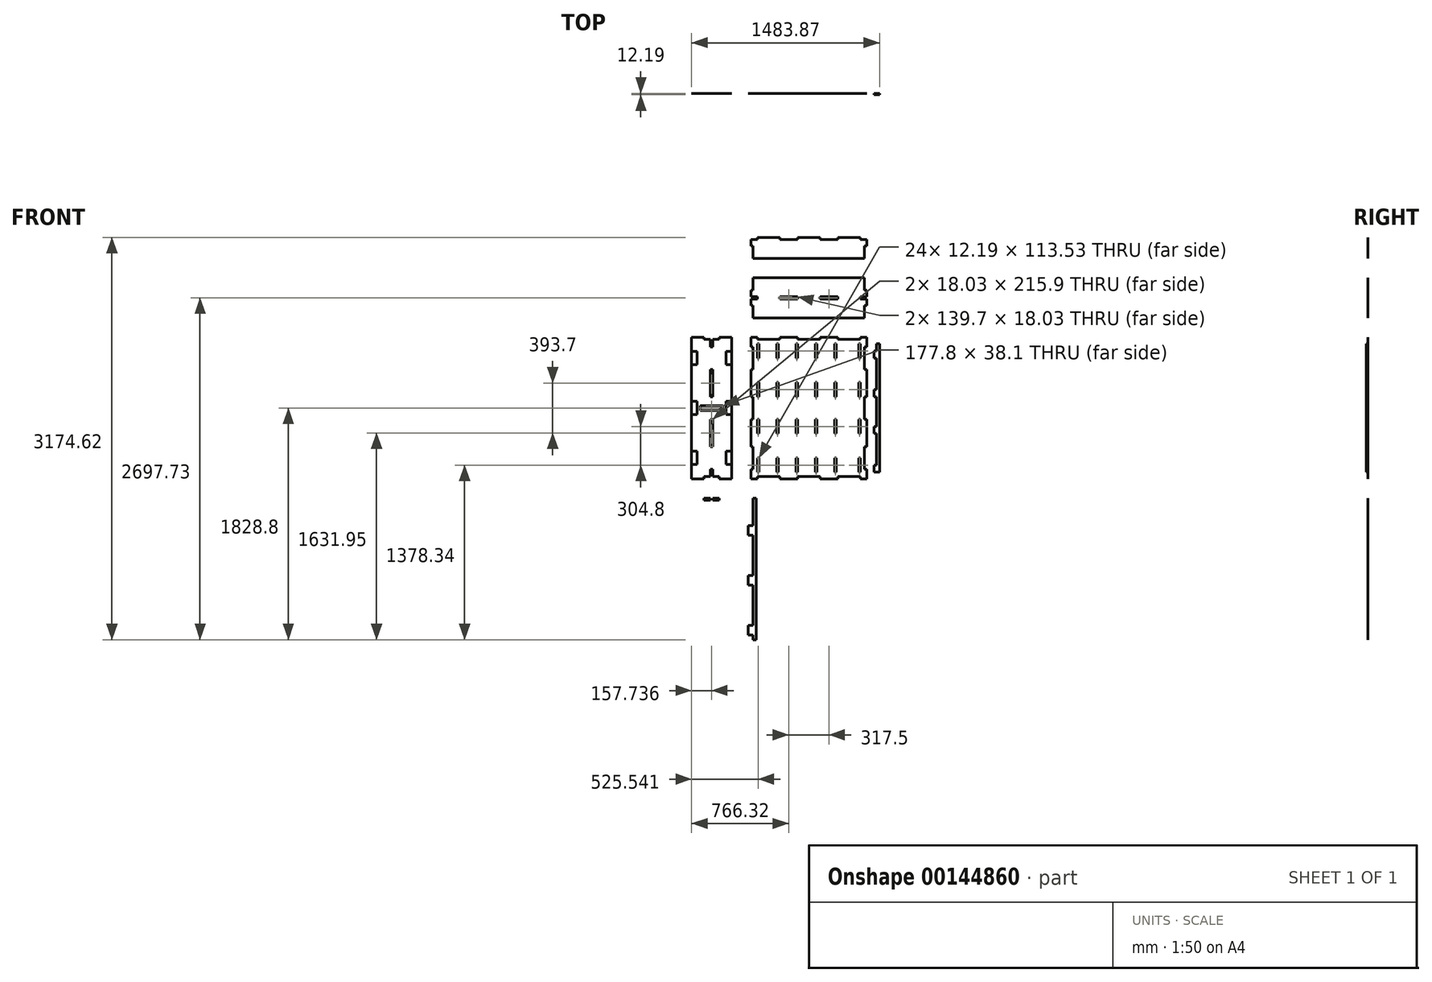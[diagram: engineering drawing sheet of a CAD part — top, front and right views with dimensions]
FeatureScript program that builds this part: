
annotation { "Feature Type Name" : "Feature", "Feature Type Description" : "" }
export const myFeature = defineFeature(function(context is Context, id is Id, definition is map)
    precondition{}
    {
        {
            assignVariable(context, id + "F0", {"name" : "ply34", "anyValue" : 0.71});
        }
        {
            var Q0;
            Q0=qCreatedBy(makeId("Front.planeOp"),FACE);
            var sketch = newSketch(context, id + "F1", { "sketchPlane" : qUnion([Q0])});
            skLineSegment(sketch, "E0.bottom", {"start": v(-457.2, 558.8) * mm, "end": v(457.2, 558.8) * mm});
            skLineSegment(sketch, "E0.top", {"start": v(-457.2, -558.8) * mm, "end": v(457.2, -558.8) * mm});
            skLineSegment(sketch, "E0.left", {"start": v(-457.2, 558.8) * mm, "end": v(-457.2, -558.8) * mm});
            skLineSegment(sketch, "E0.right", {"start": v(457.2, 558.8) * mm, "end": v(457.2, -558.8) * mm});
            skPoint(sketch, "E0.middle", {"position": v(0, 0) * mm});
            skLineSegment(sketch, "E1.bottom", {"start": v(-457.2, 482.6) * mm, "end": v(-439.17, 482.6) * mm});
            skLineSegment(sketch, "E1.top", {"start": v(-457.2, 304.8) * mm, "end": v(-439.17, 304.8) * mm});
            skLineSegment(sketch, "E1.left", {"start": v(-457.2, 482.6) * mm, "end": v(-457.2, 304.8) * mm});
            skLineSegment(sketch, "E1.right", {"start": v(-439.17, 482.6) * mm, "end": v(-439.17, 304.8) * mm});
            skLineSegment(sketch, "E2.bottom", {"start": v(-457.2, 88.9) * mm, "end": v(-439.17, 88.9) * mm});
            skLineSegment(sketch, "E2.top", {"start": v(-457.2, -88.9) * mm, "end": v(-439.17, -88.9) * mm});
            skLineSegment(sketch, "E2.left", {"start": v(-457.2, 88.9) * mm, "end": v(-457.2, -88.9) * mm});
            skLineSegment(sketch, "E2.right", {"start": v(-439.17, 88.9) * mm, "end": v(-439.17, -88.9) * mm});
            skPoint(sketch, "E3", {"position": v(-439.17, 0) * mm});
            skLineSegment(sketch, "E4", {"start": v(-457.2, 0) * mm, "end": v(457.2, 0) * mm, "construction": true});
            skLineSegment(sketch, "E5", {"start": v(0, 558.8) * mm, "end": v(0, -558.8) * mm, "construction": true});
            skLineSegment(sketch, "E6.MirrorCS", {"start": v(-457.2, -482.6) * mm, "end": v(-439.17, -482.6) * mm});
            skLineSegment(sketch, "E7.MirrorCS", {"start": v(-457.2, -304.8) * mm, "end": v(-439.17, -304.8) * mm});
            skLineSegment(sketch, "E8.MirrorCS", {"start": v(-457.2, -482.6) * mm, "end": v(-457.2, -304.8) * mm});
            skLineSegment(sketch, "E9.MirrorCS", {"start": v(-439.17, -482.6) * mm, "end": v(-439.17, -304.8) * mm});
            skLineSegment(sketch, "E10.MirrorCS", {"start": v(457.2, -88.9) * mm, "end": v(439.17, -88.9) * mm});
            skLineSegment(sketch, "E11.MirrorCS", {"start": v(457.2, 304.8) * mm, "end": v(439.17, 304.8) * mm});
            skLineSegment(sketch, "E12.MirrorCS", {"start": v(457.2, 482.6) * mm, "end": v(439.17, 482.6) * mm});
            skLineSegment(sketch, "E13.MirrorCS", {"start": v(457.2, 88.9) * mm, "end": v(439.17, 88.9) * mm});
            skLineSegment(sketch, "E14.MirrorCS", {"start": v(457.2, -304.8) * mm, "end": v(439.17, -304.8) * mm});
            skLineSegment(sketch, "E15.MirrorCS", {"start": v(457.2, -482.6) * mm, "end": v(439.17, -482.6) * mm});
            skLineSegment(sketch, "E16.MirrorCS", {"start": v(439.17, 88.9) * mm, "end": v(439.17, -88.9) * mm});
            skLineSegment(sketch, "E17.MirrorCS", {"start": v(457.2, 88.9) * mm, "end": v(457.2, -88.9) * mm});
            skLineSegment(sketch, "E18.MirrorCS", {"start": v(457.2, -482.6) * mm, "end": v(457.2, -304.8) * mm});
            skLineSegment(sketch, "E19.MirrorCS", {"start": v(439.17, -482.6) * mm, "end": v(439.17, -304.8) * mm});
            skLineSegment(sketch, "E20.MirrorCS", {"start": v(457.2, 482.6) * mm, "end": v(457.2, 304.8) * mm});
            skPoint(sketch, "E21.MirrorP", {"position": v(439.17, 0) * mm});
            skLineSegment(sketch, "E22.MirrorCS", {"start": v(439.17, 482.6) * mm, "end": v(439.17, 304.8) * mm});
            skLineSegment(sketch, "E23.bottom", {"start": v(-406.4, 558.8) * mm, "end": v(-228.6, 558.8) * mm});
            skLineSegment(sketch, "E23.top", {"start": v(-406.4, 540.77) * mm, "end": v(-228.6, 540.77) * mm});
            skLineSegment(sketch, "E23.left", {"start": v(-406.4, 558.8) * mm, "end": v(-406.4, 540.77) * mm});
            skLineSegment(sketch, "E23.right", {"start": v(-228.6, 558.8) * mm, "end": v(-228.6, 540.77) * mm});
            skLineSegment(sketch, "E24.bottom", {"start": v(-88.9, 558.8) * mm, "end": v(88.9, 558.8) * mm});
            skLineSegment(sketch, "E24.top", {"start": v(-88.9, 540.77) * mm, "end": v(88.9, 540.77) * mm});
            skLineSegment(sketch, "E24.left", {"start": v(-88.9, 558.8) * mm, "end": v(-88.9, 540.77) * mm});
            skLineSegment(sketch, "E24.right", {"start": v(88.9, 558.8) * mm, "end": v(88.9, 540.77) * mm});
            skPoint(sketch, "E25", {"position": v(0, 558.8) * mm});
            skLineSegment(sketch, "E26.MirrorCS", {"start": v(228.6, 558.8) * mm, "end": v(228.6, 540.77) * mm});
            skLineSegment(sketch, "E27.MirrorCS", {"start": v(406.4, 558.8) * mm, "end": v(406.4, 540.77) * mm});
            skLineSegment(sketch, "E28.MirrorCS", {"start": v(406.4, 540.77) * mm, "end": v(228.6, 540.77) * mm});
            skLineSegment(sketch, "E29.MirrorCS", {"start": v(406.4, 558.8) * mm, "end": v(228.6, 558.8) * mm});
            skLineSegment(sketch, "E30.MirrorCS", {"start": v(-88.9, -558.8) * mm, "end": v(88.9, -558.8) * mm});
            skLineSegment(sketch, "E31.MirrorCS", {"start": v(228.6, -558.8) * mm, "end": v(228.6, -540.77) * mm});
            skLineSegment(sketch, "E32.MirrorCS", {"start": v(-228.6, -558.8) * mm, "end": v(-228.6, -540.77) * mm});
            skLineSegment(sketch, "E33.MirrorCS", {"start": v(88.9, -558.8) * mm, "end": v(88.9, -540.77) * mm});
            skLineSegment(sketch, "E34.MirrorCS", {"start": v(-406.4, -558.8) * mm, "end": v(-406.4, -540.77) * mm});
            skLineSegment(sketch, "E35.MirrorCS", {"start": v(-88.9, -558.8) * mm, "end": v(-88.9, -540.77) * mm});
            skLineSegment(sketch, "E36.MirrorCS", {"start": v(406.4, -558.8) * mm, "end": v(406.4, -540.77) * mm});
            skLineSegment(sketch, "E37.MirrorCS", {"start": v(-406.4, -558.8) * mm, "end": v(-228.6, -558.8) * mm});
            skLineSegment(sketch, "E38.MirrorCS", {"start": v(-88.9, -540.77) * mm, "end": v(88.9, -540.77) * mm});
            skLineSegment(sketch, "E39.MirrorCS", {"start": v(-406.4, -540.77) * mm, "end": v(-228.6, -540.77) * mm});
            skLineSegment(sketch, "E40.MirrorCS", {"start": v(406.4, -558.8) * mm, "end": v(228.6, -558.8) * mm});
            skLineSegment(sketch, "E41.MirrorCS", {"start": v(406.4, -540.77) * mm, "end": v(228.6, -540.77) * mm});
            skPoint(sketch, "E42.MirrorP", {"position": v(0, -558.8) * mm});
            skLineSegment(sketch, "E43.bottom", {"start": v(-609.6, -558.8) * mm, "end": v(-925.07, -558.8) * mm});
            skLineSegment(sketch, "E43.top", {"start": v(-609.6, 558.8) * mm, "end": v(-925.07, 558.8) * mm});
            skLineSegment(sketch, "E43.left", {"start": v(-609.6, -558.8) * mm, "end": v(-609.6, 558.8) * mm});
            skLineSegment(sketch, "E43.right", {"start": v(-925.07, -558.8) * mm, "end": v(-925.07, 558.8) * mm});
            skLineSegment(sketch, "E44.bottom", {"start": v(-776.35, 558.8) * mm, "end": v(-758.32, 558.8) * mm});
            skLineSegment(sketch, "E44.top", {"start": v(-776.35, 482.6) * mm, "end": v(-758.32, 482.6) * mm});
            skLineSegment(sketch, "E44.left", {"start": v(-776.35, 558.8) * mm, "end": v(-776.35, 482.6) * mm});
            skLineSegment(sketch, "E44.right", {"start": v(-758.32, 558.8) * mm, "end": v(-758.32, 482.6) * mm});
            skPoint(sketch, "E45", {"position": v(-767.33, 558.8) * mm});
            skLineSegment(sketch, "E46.bottom", {"start": v(-776.35, 304.8) * mm, "end": v(-758.32, 304.8) * mm});
            skLineSegment(sketch, "E46.top", {"start": v(-776.35, 88.9) * mm, "end": v(-758.32, 88.9) * mm});
            skLineSegment(sketch, "E46.left", {"start": v(-776.35, 304.8) * mm, "end": v(-776.35, 88.9) * mm});
            skLineSegment(sketch, "E46.right", {"start": v(-758.32, 304.8) * mm, "end": v(-758.32, 88.9) * mm});
            skLineSegment(sketch, "E47.bottom", {"start": v(-776.35, -88.9) * mm, "end": v(-758.32, -88.9) * mm});
            skLineSegment(sketch, "E47.top", {"start": v(-776.35, -304.8) * mm, "end": v(-758.32, -304.8) * mm});
            skLineSegment(sketch, "E47.left", {"start": v(-776.35, -88.9) * mm, "end": v(-776.35, -304.8) * mm});
            skLineSegment(sketch, "E47.right", {"start": v(-758.32, -88.9) * mm, "end": v(-758.32, -304.8) * mm});
            skLineSegment(sketch, "E48.bottom", {"start": v(-776.35, -482.6) * mm, "end": v(-758.32, -482.6) * mm});
            skLineSegment(sketch, "E48.top", {"start": v(-776.35, -558.8) * mm, "end": v(-758.32, -558.8) * mm});
            skLineSegment(sketch, "E48.left", {"start": v(-776.35, -482.6) * mm, "end": v(-776.35, -558.8) * mm});
            skLineSegment(sketch, "E48.right", {"start": v(-758.32, -482.6) * mm, "end": v(-758.32, -558.8) * mm});
            skLineSegment(sketch, "E49.bottom", {"start": v(-776.35, 558.8) * mm, "end": v(-827.15, 558.8) * mm});
            skLineSegment(sketch, "E49.top", {"start": v(-776.35, 540.77) * mm, "end": v(-827.15, 540.77) * mm});
            skLineSegment(sketch, "E49.left", {"start": v(-776.35, 558.8) * mm, "end": v(-776.35, 540.77) * mm});
            skLineSegment(sketch, "E49.right", {"start": v(-827.15, 558.8) * mm, "end": v(-827.15, 540.77) * mm});
            skLineSegment(sketch, "E50.bottom", {"start": v(-758.32, 558.8) * mm, "end": v(-707.52, 558.8) * mm});
            skLineSegment(sketch, "E50.top", {"start": v(-758.32, 540.77) * mm, "end": v(-707.52, 540.77) * mm});
            skLineSegment(sketch, "E50.left", {"start": v(-758.32, 558.8) * mm, "end": v(-758.32, 540.77) * mm});
            skLineSegment(sketch, "E50.right", {"start": v(-707.52, 558.8) * mm, "end": v(-707.52, 540.77) * mm});
            skLineSegment(sketch, "E51.MirrorCS", {"start": v(-758.32, -540.77) * mm, "end": v(-707.52, -540.77) * mm});
            skLineSegment(sketch, "E52.MirrorCS", {"start": v(-758.32, -558.8) * mm, "end": v(-707.52, -558.8) * mm});
            skLineSegment(sketch, "E53.MirrorCS", {"start": v(-758.32, -558.8) * mm, "end": v(-758.32, -540.77) * mm});
            skLineSegment(sketch, "E54.MirrorCS", {"start": v(-827.15, -558.8) * mm, "end": v(-827.15, -540.77) * mm});
            skLineSegment(sketch, "E55.MirrorCS", {"start": v(-776.35, -540.77) * mm, "end": v(-827.15, -540.77) * mm});
            skPoint(sketch, "E56.MirrorP", {"position": v(-767.33, -558.8) * mm});
            skLineSegment(sketch, "E57.MirrorCS", {"start": v(-776.35, -558.8) * mm, "end": v(-776.35, -540.77) * mm});
            skLineSegment(sketch, "E58.MirrorCS", {"start": v(-776.35, -558.8) * mm, "end": v(-827.15, -558.8) * mm});
            skLineSegment(sketch, "E59.MirrorCS", {"start": v(-707.52, -558.8) * mm, "end": v(-707.52, -540.77) * mm});
            skLineSegment(sketch, "E60.bottom", {"start": v(-439.17, 1026.67) * mm, "end": v(439.17, 1026.67) * mm});
            skLineSegment(sketch, "E60.top", {"start": v(-439.17, 711.2) * mm, "end": v(439.17, 711.2) * mm});
            skLineSegment(sketch, "E60.left", {"start": v(-439.17, 1026.67) * mm, "end": v(-439.17, 711.2) * mm});
            skLineSegment(sketch, "E60.right", {"start": v(439.17, 1026.67) * mm, "end": v(439.17, 711.2) * mm});
            skLineSegment(sketch, "E61.bottom", {"start": v(-439.17, 877.95) * mm, "end": v(-457.2, 877.95) * mm});
            skLineSegment(sketch, "E61.top", {"start": v(-439.17, 928.75) * mm, "end": v(-457.2, 928.75) * mm});
            skLineSegment(sketch, "E61.left", {"start": v(-439.17, 877.95) * mm, "end": v(-439.17, 928.75) * mm});
            skLineSegment(sketch, "E61.right", {"start": v(-457.2, 877.95) * mm, "end": v(-457.2, 928.75) * mm});
            skLineSegment(sketch, "E62.bottom", {"start": v(-439.17, 859.92) * mm, "end": v(-457.2, 859.92) * mm});
            skLineSegment(sketch, "E62.top", {"start": v(-439.17, 809.12) * mm, "end": v(-457.2, 809.12) * mm});
            skLineSegment(sketch, "E62.left", {"start": v(-439.17, 859.92) * mm, "end": v(-439.17, 809.12) * mm});
            skLineSegment(sketch, "E62.right", {"start": v(-457.2, 859.92) * mm, "end": v(-457.2, 809.12) * mm});
            skLineSegment(sketch, "E63", {"start": v(-448.18, 877.95) * mm, "end": v(-448.18, 859.92) * mm, "construction": true});
            skPoint(sketch, "E64", {"position": v(-448.18, 868.93) * mm});
            skPoint(sketch, "E65", {"position": v(-439.17, 868.93) * mm});
            skLineSegment(sketch, "E66.bottom", {"start": v(-439.17, 877.95) * mm, "end": v(-406.4, 877.95) * mm});
            skLineSegment(sketch, "E66.top", {"start": v(-439.17, 859.92) * mm, "end": v(-406.4, 859.92) * mm});
            skLineSegment(sketch, "E66.left", {"start": v(-439.17, 877.95) * mm, "end": v(-439.17, 859.92) * mm});
            skLineSegment(sketch, "E66.right", {"start": v(-406.4, 877.95) * mm, "end": v(-406.4, 859.92) * mm});
            skLineSegment(sketch, "E67.bottom", {"start": v(-228.6, 877.95) * mm, "end": v(-88.9, 877.95) * mm});
            skLineSegment(sketch, "E67.top", {"start": v(-228.6, 859.92) * mm, "end": v(-88.9, 859.92) * mm});
            skLineSegment(sketch, "E67.left", {"start": v(-228.6, 877.95) * mm, "end": v(-228.6, 859.92) * mm});
            skLineSegment(sketch, "E67.right", {"start": v(-88.9, 877.95) * mm, "end": v(-88.9, 859.92) * mm});
            skLineSegment(sketch, "E68.bottom", {"start": v(88.9, 877.95) * mm, "end": v(228.6, 877.95) * mm});
            skLineSegment(sketch, "E68.top", {"start": v(88.9, 859.92) * mm, "end": v(228.6, 859.92) * mm});
            skLineSegment(sketch, "E68.left", {"start": v(88.9, 877.95) * mm, "end": v(88.9, 859.92) * mm});
            skLineSegment(sketch, "E68.right", {"start": v(228.6, 877.95) * mm, "end": v(228.6, 859.92) * mm});
            skLineSegment(sketch, "E69.MirrorCS", {"start": v(439.17, 877.95) * mm, "end": v(439.17, 859.92) * mm});
            skLineSegment(sketch, "E70.MirrorCS", {"start": v(439.17, 877.95) * mm, "end": v(457.2, 877.95) * mm});
            skLineSegment(sketch, "E71.MirrorCS", {"start": v(406.4, 877.95) * mm, "end": v(406.4, 859.92) * mm});
            skLineSegment(sketch, "E72.MirrorCS", {"start": v(439.17, 928.75) * mm, "end": v(457.2, 928.75) * mm});
            skLineSegment(sketch, "E73.MirrorCS", {"start": v(448.18, 877.95) * mm, "end": v(448.18, 859.92) * mm, "construction": true});
            skLineSegment(sketch, "E74.MirrorCS", {"start": v(439.17, 809.12) * mm, "end": v(457.2, 809.12) * mm});
            skLineSegment(sketch, "E75.MirrorCS", {"start": v(439.17, 859.92) * mm, "end": v(457.2, 859.92) * mm});
            skLineSegment(sketch, "E76.MirrorCS", {"start": v(439.17, 877.95) * mm, "end": v(406.4, 877.95) * mm});
            skLineSegment(sketch, "E77.MirrorCS", {"start": v(439.17, 859.92) * mm, "end": v(406.4, 859.92) * mm});
            skLineSegment(sketch, "E78.MirrorCS", {"start": v(439.17, 877.95) * mm, "end": v(439.17, 928.75) * mm});
            skLineSegment(sketch, "E79.MirrorCS", {"start": v(439.17, 859.92) * mm, "end": v(439.17, 809.12) * mm});
            skLineSegment(sketch, "E80.MirrorCS", {"start": v(457.2, 877.95) * mm, "end": v(457.2, 928.75) * mm});
            skPoint(sketch, "E81.MirrorP", {"position": v(439.17, 868.93) * mm});
            skLineSegment(sketch, "E82.MirrorCS", {"start": v(457.2, 859.92) * mm, "end": v(457.2, 809.12) * mm});
            skPoint(sketch, "E83.MirrorP", {"position": v(448.18, 868.93) * mm});
            skLineSegment(sketch, "E84", {"start": v(-767.33, -558.8) * mm, "end": v(-767.33, 558.8) * mm, "construction": true});
            skLineSegment(sketch, "E85", {"start": v(439.17, 1102.87) * mm, "end": v(-439.17, 1102.87) * mm, "construction": true});
            skLineSegment(sketch, "E86.MirrorCS", {"start": v(-439.17, 1179.07) * mm, "end": v(439.17, 1179.07) * mm});
            skLineSegment(sketch, "E87.MirrorCS", {"start": v(-439.17, 1179.07) * mm, "end": v(-439.17, 1345.82) * mm});
            skLineSegment(sketch, "E88.MirrorCS", {"start": v(439.17, 1179.07) * mm, "end": v(439.17, 1345.82) * mm});
            skLineSegment(sketch, "E89.MirrorCS", {"start": v(228.6, 1327.78) * mm, "end": v(228.6, 1345.82) * mm});
            skLineSegment(sketch, "E90.MirrorCS", {"start": v(-228.6, 1327.78) * mm, "end": v(-228.6, 1345.82) * mm});
            skLineSegment(sketch, "E91.MirrorCS", {"start": v(-88.9, 1327.78) * mm, "end": v(-88.9, 1345.82) * mm});
            skLineSegment(sketch, "E92.MirrorCS", {"start": v(88.9, 1327.78) * mm, "end": v(88.9, 1345.82) * mm});
            skLineSegment(sketch, "E93.MirrorCS", {"start": v(-228.6, 1345.82) * mm, "end": v(-88.9, 1345.82) * mm});
            skLineSegment(sketch, "E94.MirrorCS", {"start": v(-228.6, 1327.78) * mm, "end": v(-88.9, 1327.78) * mm});
            skLineSegment(sketch, "E95.MirrorCS", {"start": v(88.9, 1345.82) * mm, "end": v(228.6, 1345.82) * mm});
            skLineSegment(sketch, "E96.MirrorCS", {"start": v(88.9, 1327.78) * mm, "end": v(228.6, 1327.78) * mm});
            skLineSegment(sketch, "E97.MirrorCS", {"start": v(439.17, 1276.98) * mm, "end": v(457.2, 1276.98) * mm});
            skLineSegment(sketch, "E98.MirrorCS", {"start": v(457.2, 1327.78) * mm, "end": v(457.2, 1276.98) * mm});
            skLineSegment(sketch, "E99.MirrorCS", {"start": v(439.17, 1327.78) * mm, "end": v(457.2, 1327.78) * mm});
            skLineSegment(sketch, "E100.MirrorCS", {"start": v(439.17, 1327.78) * mm, "end": v(406.4, 1327.78) * mm});
            skLineSegment(sketch, "E101.MirrorCS", {"start": v(406.4, 1327.78) * mm, "end": v(406.4, 1345.82) * mm});
            skLineSegment(sketch, "E102.MirrorCS", {"start": v(439.17, 1345.82) * mm, "end": v(406.4, 1345.82) * mm});
            skLineSegment(sketch, "E103.MirrorCS", {"start": v(-439.17, 1276.98) * mm, "end": v(-457.2, 1276.98) * mm});
            skLineSegment(sketch, "E104.MirrorCS", {"start": v(-457.2, 1327.78) * mm, "end": v(-457.2, 1276.98) * mm});
            skLineSegment(sketch, "E105.MirrorCS", {"start": v(-439.17, 1327.78) * mm, "end": v(-457.2, 1327.78) * mm});
            skLineSegment(sketch, "E106.MirrorCS", {"start": v(-439.17, 1327.78) * mm, "end": v(-406.4, 1327.78) * mm});
            skLineSegment(sketch, "E107.MirrorCS", {"start": v(-406.4, 1327.78) * mm, "end": v(-406.4, 1345.82) * mm});
            skLineSegment(sketch, "E108.MirrorCS", {"start": v(-439.17, 1345.82) * mm, "end": v(-406.4, 1345.82) * mm});
            skLineSegment(sketch, "E109", {"start": v(-406.4, 1345.82) * mm, "end": v(-228.6, 1345.82) * mm});
            skLineSegment(sketch, "E110", {"start": v(-88.9, 1345.82) * mm, "end": v(88.9, 1345.82) * mm});
            skLineSegment(sketch, "E111", {"start": v(228.6, 1345.82) * mm, "end": v(406.4, 1345.82) * mm});
            skLineSegment(sketch, "E112.bottom", {"start": v(-609.6, 52.07) * mm, "end": v(-653.31, 52.07) * mm});
            skLineSegment(sketch, "E112.top", {"start": v(-609.6, -52.07) * mm, "end": v(-653.31, -52.07) * mm});
            skLineSegment(sketch, "E112.left", {"start": v(-609.6, 52.07) * mm, "end": v(-609.6, -52.07) * mm});
            skLineSegment(sketch, "E112.right", {"start": v(-653.31, 52.07) * mm, "end": v(-653.31, -52.07) * mm});
            skPoint(sketch, "E113", {"position": v(-609.6, 0) * mm});
            skLineSegment(sketch, "E114", {"start": v(-758.32, 482.6) * mm, "end": v(-758.32, 304.8) * mm, "construction": true});
            skLineSegment(sketch, "E115.bottom", {"start": v(-653.31, 341.63) * mm, "end": v(-609.6, 341.63) * mm});
            skLineSegment(sketch, "E115.top", {"start": v(-653.31, 445.77) * mm, "end": v(-609.6, 445.77) * mm});
            skLineSegment(sketch, "E115.left", {"start": v(-653.31, 341.63) * mm, "end": v(-653.31, 445.77) * mm});
            skLineSegment(sketch, "E115.right", {"start": v(-609.6, 341.63) * mm, "end": v(-609.6, 445.77) * mm});
            skPoint(sketch, "E115.middle", {"position": v(-631.46, 393.7) * mm});
            skPoint(sketch, "E115.middle.positionSnap0", {"position": v(-631.46, 52.07) * mm});
            skPoint(sketch, "E115.middle.positionSnap1", {"position": v(-758.32, 393.7) * mm});
            skPoint(sketch, "E115.centerSnap0", {"position": v(-631.46, 52.07) * mm});
            skPoint(sketch, "E115.centerSnap1", {"position": v(-758.32, 393.7) * mm});
            skLineSegment(sketch, "E116.MirrorCS", {"start": v(-653.31, -341.63) * mm, "end": v(-609.6, -341.63) * mm});
            skLineSegment(sketch, "E117.MirrorCS", {"start": v(-653.31, -445.77) * mm, "end": v(-609.6, -445.77) * mm});
            skLineSegment(sketch, "E118.MirrorCS", {"start": v(-653.31, -341.63) * mm, "end": v(-653.31, -445.77) * mm});
            skPoint(sketch, "E119.MirrorP", {"position": v(-631.46, -393.7) * mm});
            skLineSegment(sketch, "E120.MirrorCS", {"start": v(-609.6, -341.63) * mm, "end": v(-609.6, -445.77) * mm});
            skLineSegment(sketch, "E121.MirrorCS", {"start": v(-881.35, -445.77) * mm, "end": v(-925.07, -445.77) * mm});
            skLineSegment(sketch, "E122.MirrorCS", {"start": v(-881.35, -341.63) * mm, "end": v(-925.07, -341.63) * mm});
            skLineSegment(sketch, "E123.MirrorCS", {"start": v(-881.35, 445.77) * mm, "end": v(-925.07, 445.77) * mm});
            skLineSegment(sketch, "E124.MirrorCS", {"start": v(-881.35, 341.63) * mm, "end": v(-925.07, 341.63) * mm});
            skLineSegment(sketch, "E125.MirrorCS", {"start": v(-925.07, -52.07) * mm, "end": v(-881.35, -52.07) * mm});
            skLineSegment(sketch, "E126.MirrorCS", {"start": v(-925.07, 52.07) * mm, "end": v(-881.35, 52.07) * mm});
            skLineSegment(sketch, "E127.MirrorCS", {"start": v(-925.07, -341.63) * mm, "end": v(-925.07, -445.77) * mm});
            skPoint(sketch, "E128.MirrorP", {"position": v(-903.21, 52.07) * mm});
            skLineSegment(sketch, "E129.MirrorCS", {"start": v(-881.35, -341.63) * mm, "end": v(-881.35, -445.77) * mm});
            skLineSegment(sketch, "E130.MirrorCS", {"start": v(-925.07, 341.63) * mm, "end": v(-925.07, 445.77) * mm});
            skLineSegment(sketch, "E131.MirrorCS", {"start": v(-881.35, 341.63) * mm, "end": v(-881.35, 445.77) * mm});
            skLineSegment(sketch, "E132.MirrorCS", {"start": v(-925.07, 52.07) * mm, "end": v(-925.07, -52.07) * mm});
            skLineSegment(sketch, "E133.MirrorCS", {"start": v(-881.35, 52.07) * mm, "end": v(-881.35, -52.07) * mm});
            skPoint(sketch, "E134.MirrorP", {"position": v(-903.21, 393.7) * mm});
            skPoint(sketch, "E135.MirrorP", {"position": v(-925.07, 0) * mm});
            skPoint(sketch, "E136.MirrorP", {"position": v(-903.21, -393.7) * mm});
            skLineSegment(sketch, "E137.bottom", {"start": v(-405.63, 507.23) * mm, "end": v(405.63, 507.23) * mm, "construction": true});
            skLineSegment(sketch, "E137.top", {"start": v(-405.63, -507.23) * mm, "end": v(405.63, -507.23) * mm, "construction": true});
            skLineSegment(sketch, "E137.left", {"start": v(-405.63, 507.23) * mm, "end": v(-405.63, -507.23) * mm, "construction": true});
            skLineSegment(sketch, "E137.right", {"start": v(405.63, 507.23) * mm, "end": v(405.63, -507.23) * mm, "construction": true});
            skLineSegment(sketch, "E138.0", {"start": v(-393.43, 495.03) * mm, "end": v(393.43, 495.03) * mm, "construction": true});
            skLineSegment(sketch, "E138.1", {"start": v(-393.43, 495.03) * mm, "end": v(-393.43, -495.03) * mm, "construction": true});
            skLineSegment(sketch, "E138.2", {"start": v(-393.43, -495.03) * mm, "end": v(393.43, -495.03) * mm, "construction": true});
            skLineSegment(sketch, "E138.3", {"start": v(393.43, 495.03) * mm, "end": v(393.43, -495.03) * mm, "construction": true});
            skPoint(sketch, "E139.oppositeSnap0", {"position": v(-439.17, 393.7) * mm});
            skLineSegment(sketch, "E139.bottom", {"start": v(-405.63, 507.23) * mm, "end": v(-393.43, 507.23) * mm});
            skLineSegment(sketch, "E139.top", {"start": v(-405.63, 393.7) * mm, "end": v(-393.43, 393.7) * mm});
            skLineSegment(sketch, "E139.left", {"start": v(-405.63, 507.23) * mm, "end": v(-405.63, 393.7) * mm});
            skLineSegment(sketch, "E139.right", {"start": v(-393.43, 507.23) * mm, "end": v(-393.43, 393.7) * mm});
            skPoint(sketch, "E140.oppositeSnap0", {"position": v(-439.17, -393.7) * mm});
            skLineSegment(sketch, "E140.bottom", {"start": v(-405.63, -507.23) * mm, "end": v(-393.43, -507.23) * mm});
            skLineSegment(sketch, "E140.top", {"start": v(-405.63, -393.7) * mm, "end": v(-393.43, -393.7) * mm});
            skLineSegment(sketch, "E140.left", {"start": v(-405.63, -507.23) * mm, "end": v(-405.63, -393.7) * mm});
            skLineSegment(sketch, "E140.right", {"start": v(-393.43, -507.23) * mm, "end": v(-393.43, -393.7) * mm});
            skLineSegment(sketch, "E141.bottom", {"start": v(-405.63, 88.9) * mm, "end": v(-393.43, 88.9) * mm});
            skLineSegment(sketch, "E141.top", {"start": v(-405.63, 202.43) * mm, "end": v(-393.43, 202.43) * mm});
            skLineSegment(sketch, "E141.left", {"start": v(-405.63, 88.9) * mm, "end": v(-405.63, 202.43) * mm});
            skLineSegment(sketch, "E141.right", {"start": v(-393.43, 88.9) * mm, "end": v(-393.43, 202.43) * mm});
            skLineSegment(sketch, "E142.bottom", {"start": v(-405.63, -88.9) * mm, "end": v(-393.43, -88.9) * mm});
            skLineSegment(sketch, "E142.top", {"start": v(-405.63, -202.43) * mm, "end": v(-393.43, -202.43) * mm});
            skLineSegment(sketch, "E142.left", {"start": v(-405.63, -88.9) * mm, "end": v(-405.63, -202.43) * mm});
            skLineSegment(sketch, "E142.right", {"start": v(-393.43, -88.9) * mm, "end": v(-393.43, -202.43) * mm});
            skLineSegment(sketch, "E143.1.0.0", {"start": v(-253.23, -507.23) * mm, "end": v(-253.23, -393.7) * mm});
            skLineSegment(sketch, "E143.1.0.1", {"start": v(-241.03, -507.23) * mm, "end": v(-241.03, -393.7) * mm});
            skLineSegment(sketch, "E143.1.0.2", {"start": v(-253.23, -507.23) * mm, "end": v(-241.03, -507.23) * mm});
            skLineSegment(sketch, "E143.1.0.3", {"start": v(-253.23, -393.7) * mm, "end": v(-241.03, -393.7) * mm});
            skLineSegment(sketch, "E143.1.0.4", {"start": v(-253.23, -88.9) * mm, "end": v(-241.03, -88.9) * mm});
            skLineSegment(sketch, "E143.1.0.5", {"start": v(-253.23, -202.43) * mm, "end": v(-241.03, -202.43) * mm});
            skLineSegment(sketch, "E143.1.0.6", {"start": v(-253.23, -88.9) * mm, "end": v(-253.23, -202.43) * mm});
            skLineSegment(sketch, "E143.1.0.7", {"start": v(-241.03, -88.9) * mm, "end": v(-241.03, -202.43) * mm});
            skLineSegment(sketch, "E143.1.0.8", {"start": v(-253.23, 88.9) * mm, "end": v(-253.23, 202.43) * mm});
            skLineSegment(sketch, "E143.1.0.9", {"start": v(-241.03, 88.9) * mm, "end": v(-241.03, 202.43) * mm});
            skLineSegment(sketch, "E143.1.0.10", {"start": v(-253.23, 88.9) * mm, "end": v(-241.03, 88.9) * mm});
            skLineSegment(sketch, "E143.1.0.11", {"start": v(-253.23, 202.43) * mm, "end": v(-241.03, 202.43) * mm});
            skLineSegment(sketch, "E143.1.0.12", {"start": v(-253.23, 507.23) * mm, "end": v(-241.03, 507.23) * mm});
            skLineSegment(sketch, "E143.1.0.13", {"start": v(-253.23, 393.7) * mm, "end": v(-241.03, 393.7) * mm});
            skLineSegment(sketch, "E143.1.0.14", {"start": v(-253.23, 507.23) * mm, "end": v(-253.23, 393.7) * mm});
            skLineSegment(sketch, "E143.1.0.15", {"start": v(-241.03, 507.23) * mm, "end": v(-241.03, 393.7) * mm});
            skLineSegment(sketch, "E143.2.0.0", {"start": v(-100.83, -507.23) * mm, "end": v(-100.83, -393.7) * mm});
            skLineSegment(sketch, "E143.2.0.1", {"start": v(-88.63, -507.23) * mm, "end": v(-88.63, -393.7) * mm});
            skLineSegment(sketch, "E143.2.0.2", {"start": v(-100.83, -507.23) * mm, "end": v(-88.63, -507.23) * mm});
            skLineSegment(sketch, "E143.2.0.3", {"start": v(-100.83, -393.7) * mm, "end": v(-88.63, -393.7) * mm});
            skLineSegment(sketch, "E143.2.0.4", {"start": v(-100.83, -88.9) * mm, "end": v(-88.63, -88.9) * mm});
            skLineSegment(sketch, "E143.2.0.5", {"start": v(-100.83, -202.43) * mm, "end": v(-88.63, -202.43) * mm});
            skLineSegment(sketch, "E143.2.0.6", {"start": v(-100.83, -88.9) * mm, "end": v(-100.83, -202.43) * mm});
            skLineSegment(sketch, "E143.2.0.7", {"start": v(-88.63, -88.9) * mm, "end": v(-88.63, -202.43) * mm});
            skLineSegment(sketch, "E143.2.0.8", {"start": v(-100.83, 88.9) * mm, "end": v(-100.83, 202.43) * mm});
            skLineSegment(sketch, "E143.2.0.9", {"start": v(-88.63, 88.9) * mm, "end": v(-88.63, 202.43) * mm});
            skLineSegment(sketch, "E143.2.0.10", {"start": v(-100.83, 88.9) * mm, "end": v(-88.63, 88.9) * mm});
            skLineSegment(sketch, "E143.2.0.11", {"start": v(-100.83, 202.43) * mm, "end": v(-88.63, 202.43) * mm});
            skLineSegment(sketch, "E143.2.0.12", {"start": v(-100.83, 507.23) * mm, "end": v(-88.63, 507.23) * mm});
            skLineSegment(sketch, "E143.2.0.13", {"start": v(-100.83, 393.7) * mm, "end": v(-88.63, 393.7) * mm});
            skLineSegment(sketch, "E143.2.0.14", {"start": v(-100.83, 507.23) * mm, "end": v(-100.83, 393.7) * mm});
            skLineSegment(sketch, "E143.2.0.15", {"start": v(-88.63, 507.23) * mm, "end": v(-88.63, 393.7) * mm});
            skLineSegment(sketch, "E143.3.0.0", {"start": v(51.57, -507.23) * mm, "end": v(51.57, -393.7) * mm});
            skLineSegment(sketch, "E143.3.0.1", {"start": v(63.77, -507.23) * mm, "end": v(63.77, -393.7) * mm});
            skLineSegment(sketch, "E143.3.0.2", {"start": v(51.57, -507.23) * mm, "end": v(63.77, -507.23) * mm});
            skLineSegment(sketch, "E143.3.0.3", {"start": v(51.57, -393.7) * mm, "end": v(63.77, -393.7) * mm});
            skLineSegment(sketch, "E143.3.0.4", {"start": v(51.57, -88.9) * mm, "end": v(63.77, -88.9) * mm});
            skLineSegment(sketch, "E143.3.0.5", {"start": v(51.57, -202.43) * mm, "end": v(63.77, -202.43) * mm});
            skLineSegment(sketch, "E143.3.0.6", {"start": v(51.57, -88.9) * mm, "end": v(51.57, -202.43) * mm});
            skLineSegment(sketch, "E143.3.0.7", {"start": v(63.77, -88.9) * mm, "end": v(63.77, -202.43) * mm});
            skLineSegment(sketch, "E143.3.0.8", {"start": v(51.57, 88.9) * mm, "end": v(51.57, 202.43) * mm});
            skLineSegment(sketch, "E143.3.0.9", {"start": v(63.77, 88.9) * mm, "end": v(63.77, 202.43) * mm});
            skLineSegment(sketch, "E143.3.0.10", {"start": v(51.57, 88.9) * mm, "end": v(63.77, 88.9) * mm});
            skLineSegment(sketch, "E143.3.0.11", {"start": v(51.57, 202.43) * mm, "end": v(63.77, 202.43) * mm});
            skLineSegment(sketch, "E143.3.0.12", {"start": v(51.57, 507.23) * mm, "end": v(63.77, 507.23) * mm});
            skLineSegment(sketch, "E143.3.0.13", {"start": v(51.57, 393.7) * mm, "end": v(63.77, 393.7) * mm});
            skLineSegment(sketch, "E143.3.0.14", {"start": v(51.57, 507.23) * mm, "end": v(51.57, 393.7) * mm});
            skLineSegment(sketch, "E143.3.0.15", {"start": v(63.77, 507.23) * mm, "end": v(63.77, 393.7) * mm});
            skLineSegment(sketch, "E143.4.0.0", {"start": v(203.97, -507.23) * mm, "end": v(203.97, -393.7) * mm});
            skLineSegment(sketch, "E143.4.0.1", {"start": v(216.17, -507.23) * mm, "end": v(216.17, -393.7) * mm});
            skLineSegment(sketch, "E143.4.0.2", {"start": v(203.97, -507.23) * mm, "end": v(216.17, -507.23) * mm});
            skLineSegment(sketch, "E143.4.0.3", {"start": v(203.97, -393.7) * mm, "end": v(216.17, -393.7) * mm});
            skLineSegment(sketch, "E143.4.0.4", {"start": v(203.97, -88.9) * mm, "end": v(216.17, -88.9) * mm});
            skLineSegment(sketch, "E143.4.0.5", {"start": v(203.97, -202.43) * mm, "end": v(216.17, -202.43) * mm});
            skLineSegment(sketch, "E143.4.0.6", {"start": v(203.97, -88.9) * mm, "end": v(203.97, -202.43) * mm});
            skLineSegment(sketch, "E143.4.0.7", {"start": v(216.17, -88.9) * mm, "end": v(216.17, -202.43) * mm});
            skLineSegment(sketch, "E143.4.0.8", {"start": v(203.97, 88.9) * mm, "end": v(203.97, 202.43) * mm});
            skLineSegment(sketch, "E143.4.0.9", {"start": v(216.17, 88.9) * mm, "end": v(216.17, 202.43) * mm});
            skLineSegment(sketch, "E143.4.0.10", {"start": v(203.97, 88.9) * mm, "end": v(216.17, 88.9) * mm});
            skLineSegment(sketch, "E143.4.0.11", {"start": v(203.97, 202.43) * mm, "end": v(216.17, 202.43) * mm});
            skLineSegment(sketch, "E143.4.0.12", {"start": v(203.97, 507.23) * mm, "end": v(216.17, 507.23) * mm});
            skLineSegment(sketch, "E143.4.0.13", {"start": v(203.97, 393.7) * mm, "end": v(216.17, 393.7) * mm});
            skLineSegment(sketch, "E143.4.0.14", {"start": v(203.97, 507.23) * mm, "end": v(203.97, 393.7) * mm});
            skLineSegment(sketch, "E143.4.0.15", {"start": v(216.17, 507.23) * mm, "end": v(216.17, 393.7) * mm});
            skLineSegment(sketch, "E143.direction1", {"start": v(-405.63, -507.23) * mm, "end": v(-253.23, -507.23) * mm, "construction": true});
            skLineSegment(sketch, "E144.MirrorCS", {"start": v(405.63, 507.23) * mm, "end": v(393.43, 507.23) * mm});
            skLineSegment(sketch, "E145.MirrorCS", {"start": v(405.63, 393.7) * mm, "end": v(393.43, 393.7) * mm});
            skLineSegment(sketch, "E146.MirrorCS", {"start": v(405.63, 507.23) * mm, "end": v(405.63, 393.7) * mm});
            skLineSegment(sketch, "E147.MirrorCS", {"start": v(393.43, 507.23) * mm, "end": v(393.43, 393.7) * mm});
            skLineSegment(sketch, "E148.MirrorCS", {"start": v(405.63, -202.43) * mm, "end": v(393.43, -202.43) * mm});
            skLineSegment(sketch, "E149.MirrorCS", {"start": v(405.63, -88.9) * mm, "end": v(393.43, -88.9) * mm});
            skLineSegment(sketch, "E150.MirrorCS", {"start": v(405.63, 88.9) * mm, "end": v(393.43, 88.9) * mm});
            skLineSegment(sketch, "E151.MirrorCS", {"start": v(405.63, 202.43) * mm, "end": v(393.43, 202.43) * mm});
            skLineSegment(sketch, "E152.MirrorCS", {"start": v(393.43, 88.9) * mm, "end": v(393.43, 202.43) * mm});
            skLineSegment(sketch, "E153.MirrorCS", {"start": v(393.43, -88.9) * mm, "end": v(393.43, -202.43) * mm});
            skLineSegment(sketch, "E154.MirrorCS", {"start": v(405.63, -88.9) * mm, "end": v(405.63, -202.43) * mm});
            skLineSegment(sketch, "E155.MirrorCS", {"start": v(405.63, 88.9) * mm, "end": v(405.63, 202.43) * mm});
            skLineSegment(sketch, "E156.MirrorCS", {"start": v(393.43, -507.23) * mm, "end": v(393.43, -393.7) * mm});
            skLineSegment(sketch, "E157.MirrorCS", {"start": v(405.63, -507.23) * mm, "end": v(405.63, -393.7) * mm});
            skLineSegment(sketch, "E158.MirrorCS", {"start": v(405.63, -507.23) * mm, "end": v(393.43, -507.23) * mm});
            skLineSegment(sketch, "E159.MirrorCS", {"start": v(405.63, -393.7) * mm, "end": v(393.43, -393.7) * mm});
            skLineSegment(sketch, "E160.bottom", {"start": v(533.4, 507.23) * mm, "end": v(558.8, 507.23) * mm});
            skLineSegment(sketch, "E160.top", {"start": v(533.4, -507.23) * mm, "end": v(558.8, -507.23) * mm});
            skLineSegment(sketch, "E160.left", {"start": v(533.4, 507.23) * mm, "end": v(533.4, -507.23) * mm});
            skLineSegment(sketch, "E160.right", {"start": v(558.8, 507.23) * mm, "end": v(558.8, -507.23) * mm});
            skPoint(sketch, "E161.startSnap0", {"position": v(405.63, 450.46) * mm});
            skPoint(sketch, "E162.endSnap0", {"position": v(533.4, 0) * mm});
            skLineSegment(sketch, "E163", {"start": v(533.4, 88.9) * mm, "end": v(515.37, 88.9) * mm});
            skLineSegment(sketch, "E164", {"start": v(515.37, 88.9) * mm, "end": v(515.37, 145.66) * mm});
            skPoint(sketch, "E164.endSnap0", {"position": v(405.63, 145.66) * mm});
            skLineSegment(sketch, "E165", {"start": v(533.4, 145.66) * mm, "end": v(515.37, 145.66) * mm});
            skLineSegment(sketch, "E166", {"start": v(533.4, 393.7) * mm, "end": v(515.37, 393.7) * mm});
            skPoint(sketch, "E166.startSnap0", {"position": v(457.2, 393.7) * mm});
            skLineSegment(sketch, "E167", {"start": v(515.37, 393.7) * mm, "end": v(515.37, 450.46) * mm});
            skLineSegment(sketch, "E168", {"start": v(533.4, 450.46) * mm, "end": v(515.37, 450.46) * mm});
            skLineSegment(sketch, "E169", {"start": v(533.4, -202.43) * mm, "end": v(515.37, -202.43) * mm});
            skLineSegment(sketch, "E170", {"start": v(515.37, -202.43) * mm, "end": v(515.37, -145.66) * mm});
            skPoint(sketch, "E170.endSnap0", {"position": v(405.63, -145.66) * mm});
            skLineSegment(sketch, "E171", {"start": v(533.4, -145.66) * mm, "end": v(515.37, -145.66) * mm});
            skLineSegment(sketch, "E172", {"start": v(533.4, -507.23) * mm, "end": v(515.37, -507.23) * mm});
            skLineSegment(sketch, "E173", {"start": v(515.37, -507.23) * mm, "end": v(515.37, -450.46) * mm});
            skPoint(sketch, "E174", {"position": v(405.63, -450.46) * mm});
            skLineSegment(sketch, "E175", {"start": v(533.4, -450.46) * mm, "end": v(515.37, -450.46) * mm});
            skLineSegment(sketch, "E176.bottom", {"start": v(-940.94, -711.2) * mm, "end": v(-593.72, -711.2) * mm});
            skLineSegment(sketch, "E176.top", {"start": v(-940.94, -1828.8) * mm, "end": v(-593.72, -1828.8) * mm});
            skLineSegment(sketch, "E176.left", {"start": v(-940.94, -711.2) * mm, "end": v(-940.94, -1828.8) * mm});
            skLineSegment(sketch, "E176.right", {"start": v(-593.72, -711.2) * mm, "end": v(-593.72, -1828.8) * mm});
            skPoint(sketch, "E177", {"position": v(-767.33, -711.2) * mm});
            skLineSegment(sketch, "E178", {"start": v(-925.07, -635) * mm, "end": v(-703.26, -635) * mm, "construction": true});
            skLineSegment(sketch, "E179.MirrorCS", {"start": v(-881.35, -1715.77) * mm, "end": v(-925.07, -1715.77) * mm, "construction": true});
            skLineSegment(sketch, "E180.MirrorCS", {"start": v(-881.35, -1611.63) * mm, "end": v(-925.07, -1611.63) * mm, "construction": true});
            skLineSegment(sketch, "E181.MirrorCS", {"start": v(-653.31, -1611.63) * mm, "end": v(-609.6, -1611.63) * mm, "construction": true});
            skLineSegment(sketch, "E182.MirrorCS", {"start": v(-653.31, -1715.77) * mm, "end": v(-609.6, -1715.77) * mm, "construction": true});
            skLineSegment(sketch, "E183.MirrorCS", {"start": v(-609.6, -1322.07) * mm, "end": v(-653.31, -1322.07) * mm, "construction": true});
            skLineSegment(sketch, "E184.MirrorCS", {"start": v(-925.07, -1322.07) * mm, "end": v(-881.35, -1322.07) * mm, "construction": true});
            skLineSegment(sketch, "E185.MirrorCS", {"start": v(-925.07, -1217.93) * mm, "end": v(-881.35, -1217.93) * mm, "construction": true});
            skLineSegment(sketch, "E186.MirrorCS", {"start": v(-609.6, -1217.93) * mm, "end": v(-653.31, -1217.93) * mm, "construction": true});
            skLineSegment(sketch, "E187.MirrorCS", {"start": v(-881.35, -928.37) * mm, "end": v(-925.07, -928.37) * mm, "construction": true});
            skLineSegment(sketch, "E188.MirrorCS", {"start": v(-881.35, -824.23) * mm, "end": v(-925.07, -824.23) * mm, "construction": true});
            skLineSegment(sketch, "E189.MirrorCS", {"start": v(-653.31, -928.37) * mm, "end": v(-609.6, -928.37) * mm, "construction": true});
            skLineSegment(sketch, "E190.MirrorCS", {"start": v(-653.31, -824.23) * mm, "end": v(-609.6, -824.23) * mm, "construction": true});
            skPoint(sketch, "E191.endSnap0", {"position": v(-903.21, -1322.07) * mm});
            skLineSegment(sketch, "E192.bottom", {"start": v(-940.94, -824.23) * mm, "end": v(-915.54, -824.23) * mm});
            skLineSegment(sketch, "E192.top", {"start": v(-940.94, -928.37) * mm, "end": v(-915.54, -928.37) * mm});
            skLineSegment(sketch, "E192.left", {"start": v(-940.94, -824.23) * mm, "end": v(-940.94, -928.37) * mm});
            skLineSegment(sketch, "E192.right", {"start": v(-915.54, -824.23) * mm, "end": v(-915.54, -928.37) * mm});
            skLineSegment(sketch, "E193.bottom", {"start": v(-940.94, -1004.57) * mm, "end": v(-922.9, -1004.57) * mm});
            skLineSegment(sketch, "E193.top", {"start": v(-940.94, -928.37) * mm, "end": v(-922.9, -928.37) * mm});
            skLineSegment(sketch, "E193.left", {"start": v(-940.94, -1004.57) * mm, "end": v(-940.94, -928.37) * mm});
            skLineSegment(sketch, "E193.right", {"start": v(-922.9, -1004.57) * mm, "end": v(-922.9, -928.37) * mm});
            skLineSegment(sketch, "E194", {"start": v(-940.94, -1270) * mm, "end": v(-593.72, -1270) * mm, "construction": true});
            skLineSegment(sketch, "E195", {"start": v(-767.33, -711.2) * mm, "end": v(-767.33, -1828.8) * mm, "construction": true});
            skLineSegment(sketch, "E196.MirrorCS", {"start": v(-593.73, -928.37) * mm, "end": v(-619.12, -928.37) * mm});
            skLineSegment(sketch, "E197.MirrorCS", {"start": v(-593.73, -928.37) * mm, "end": v(-611.76, -928.37) * mm});
            skLineSegment(sketch, "E198.MirrorCS", {"start": v(-593.73, -1004.57) * mm, "end": v(-611.76, -1004.57) * mm});
            skLineSegment(sketch, "E199.MirrorCS", {"start": v(-593.72, -824.23) * mm, "end": v(-619.12, -824.23) * mm});
            skLineSegment(sketch, "E200.MirrorCS", {"start": v(-611.76, -1004.57) * mm, "end": v(-611.76, -928.37) * mm});
            skLineSegment(sketch, "E201.MirrorCS", {"start": v(-593.72, -1004.57) * mm, "end": v(-593.72, -928.37) * mm});
            skLineSegment(sketch, "E202.MirrorCS", {"start": v(-593.72, -824.23) * mm, "end": v(-593.72, -928.37) * mm});
            skLineSegment(sketch, "E203.MirrorCS", {"start": v(-619.12, -824.23) * mm, "end": v(-619.12, -928.37) * mm});
            skLineSegment(sketch, "E204.MirrorCS", {"start": v(-940.94, -1611.63) * mm, "end": v(-915.54, -1611.63) * mm});
            skLineSegment(sketch, "E205.MirrorCS", {"start": v(-940.94, -1715.77) * mm, "end": v(-915.54, -1715.77) * mm});
            skLineSegment(sketch, "E206.MirrorCS", {"start": v(-940.94, -1715.77) * mm, "end": v(-940.94, -1611.63) * mm});
            skLineSegment(sketch, "E207.MirrorCS", {"start": v(-915.54, -1715.77) * mm, "end": v(-915.54, -1611.63) * mm});
            skLineSegment(sketch, "E208.MirrorCS", {"start": v(-593.73, -1611.63) * mm, "end": v(-619.12, -1611.63) * mm});
            skLineSegment(sketch, "E209.MirrorCS", {"start": v(-593.72, -1715.77) * mm, "end": v(-593.72, -1611.63) * mm});
            skLineSegment(sketch, "E210.MirrorCS", {"start": v(-619.12, -1715.77) * mm, "end": v(-619.12, -1611.63) * mm});
            skLineSegment(sketch, "E211.MirrorCS", {"start": v(-593.72, -1715.77) * mm, "end": v(-619.12, -1715.77) * mm});
            skLineSegment(sketch, "E212", {"start": v(-903.21, -1322.07) * mm, "end": v(-903.21, -1611.63) * mm, "construction": true});
            skLineSegment(sketch, "E213", {"start": v(-903.21, -1466.85) * mm, "end": v(-767.33, -1466.85) * mm, "construction": true});
            skLineSegment(sketch, "E214.MirrorCS", {"start": v(-940.94, -1322.07) * mm, "end": v(-915.54, -1322.07) * mm});
            skLineSegment(sketch, "E215.MirrorCS", {"start": v(-940.94, -1217.93) * mm, "end": v(-915.54, -1217.93) * mm});
            skLineSegment(sketch, "E216.MirrorCS", {"start": v(-940.94, -1217.93) * mm, "end": v(-940.94, -1322.07) * mm});
            skLineSegment(sketch, "E217.MirrorCS", {"start": v(-915.54, -1217.93) * mm, "end": v(-915.54, -1322.07) * mm});
            skLineSegment(sketch, "E218.bottom", {"start": v(-593.72, -1217.93) * mm, "end": v(-619.12, -1217.93) * mm});
            skLineSegment(sketch, "E218.top", {"start": v(-593.72, -1322.07) * mm, "end": v(-619.12, -1322.07) * mm});
            skLineSegment(sketch, "E218.left", {"start": v(-593.72, -1217.93) * mm, "end": v(-593.72, -1322.07) * mm});
            skLineSegment(sketch, "E218.right", {"start": v(-619.12, -1217.93) * mm, "end": v(-619.12, -1322.07) * mm});
            skLineSegment(sketch, "E219.bottom", {"start": v(-593.72, -1398.27) * mm, "end": v(-611.76, -1398.27) * mm});
            skLineSegment(sketch, "E219.top", {"start": v(-593.72, -1322.07) * mm, "end": v(-611.76, -1322.07) * mm});
            skLineSegment(sketch, "E219.left", {"start": v(-593.72, -1398.27) * mm, "end": v(-593.72, -1322.07) * mm});
            skLineSegment(sketch, "E219.right", {"start": v(-611.76, -1398.27) * mm, "end": v(-611.76, -1322.07) * mm});
            skLineSegment(sketch, "E220.bottom", {"start": v(-441.32, -928.37) * mm, "end": v(-415.92, -928.37) * mm});
            skLineSegment(sketch, "E220.top", {"start": v(-441.32, -1791.97) * mm, "end": v(-415.92, -1791.97) * mm});
            skLineSegment(sketch, "E220.left", {"start": v(-441.32, -928.37) * mm, "end": v(-441.32, -1791.97) * mm});
            skLineSegment(sketch, "E220.right", {"start": v(-415.92, -928.37) * mm, "end": v(-415.92, -1791.97) * mm});
            skLineSegment(sketch, "E221.bottom", {"start": v(-940.94, -1398.27) * mm, "end": v(-922.9, -1398.27) * mm});
            skLineSegment(sketch, "E221.top", {"start": v(-940.94, -1322.07) * mm, "end": v(-922.9, -1322.07) * mm});
            skLineSegment(sketch, "E221.left", {"start": v(-940.94, -1398.27) * mm, "end": v(-940.94, -1322.07) * mm});
            skLineSegment(sketch, "E221.right", {"start": v(-922.9, -1398.27) * mm, "end": v(-922.9, -1322.07) * mm});
            skLineSegment(sketch, "E222.bottom", {"start": v(-940.94, -1791.97) * mm, "end": v(-922.9, -1791.97) * mm});
            skLineSegment(sketch, "E222.top", {"start": v(-940.94, -1715.77) * mm, "end": v(-922.9, -1715.77) * mm});
            skLineSegment(sketch, "E222.left", {"start": v(-940.94, -1791.97) * mm, "end": v(-940.94, -1715.77) * mm});
            skLineSegment(sketch, "E222.right", {"start": v(-922.9, -1791.97) * mm, "end": v(-922.9, -1715.77) * mm});
            skLineSegment(sketch, "E223.MirrorCS", {"start": v(-593.72, -1791.97) * mm, "end": v(-611.76, -1791.97) * mm});
            skLineSegment(sketch, "E224.MirrorCS", {"start": v(-593.72, -1791.97) * mm, "end": v(-593.72, -1715.77) * mm});
            skLineSegment(sketch, "E225.MirrorCS", {"start": v(-593.72, -1715.77) * mm, "end": v(-611.76, -1715.77) * mm});
            skLineSegment(sketch, "E226.MirrorCS", {"start": v(-611.76, -1791.97) * mm, "end": v(-611.76, -1715.77) * mm});
            skLineSegment(sketch, "E227", {"start": v(-441.32, -928.37) * mm, "end": v(-478.4, -928.37) * mm});
            skLineSegment(sketch, "E228", {"start": v(-478.4, -928.37) * mm, "end": v(-478.4, -1004.57) * mm});
            skLineSegment(sketch, "E229", {"start": v(-478.4, -1004.57) * mm, "end": v(-441.32, -1004.57) * mm});
            skLineSegment(sketch, "E230", {"start": v(-441.32, -1322.07) * mm, "end": v(-478.4, -1322.07) * mm});
            skLineSegment(sketch, "E231", {"start": v(-478.4, -1322.07) * mm, "end": v(-478.4, -1398.27) * mm});
            skLineSegment(sketch, "E232", {"start": v(-478.4, -1398.27) * mm, "end": v(-441.32, -1398.27) * mm});
            skLineSegment(sketch, "E233", {"start": v(-441.32, -1791.97) * mm, "end": v(-478.4, -1791.97) * mm});
            skLineSegment(sketch, "E234", {"start": v(-478.4, -1791.97) * mm, "end": v(-478.4, -1715.77) * mm});
            skLineSegment(sketch, "E235", {"start": v(-478.4, -1715.77) * mm, "end": v(-441.32, -1715.77) * mm});
            skLineSegment(sketch, "E236.MirrorCS", {"start": v(-776.35, -711.2) * mm, "end": v(-758.32, -711.2) * mm});
            skLineSegment(sketch, "E237.MirrorCS", {"start": v(-776.35, -711.2) * mm, "end": v(-776.35, -729.23) * mm});
            skLineSegment(sketch, "E238.MirrorCS", {"start": v(-827.15, -711.2) * mm, "end": v(-827.15, -729.23) * mm});
            skLineSegment(sketch, "E239.MirrorCS", {"start": v(-707.52, -711.2) * mm, "end": v(-707.52, -729.23) * mm});
            skLineSegment(sketch, "E240.MirrorCS", {"start": v(-758.32, -711.2) * mm, "end": v(-758.32, -729.23) * mm});
            skLineSegment(sketch, "E241.MirrorCS", {"start": v(-758.32, -729.23) * mm, "end": v(-707.52, -729.23) * mm});
            skLineSegment(sketch, "E242.MirrorCS", {"start": v(-776.35, -787.4) * mm, "end": v(-776.35, -711.2) * mm});
            skLineSegment(sketch, "E243.MirrorCS", {"start": v(-776.35, -729.23) * mm, "end": v(-827.15, -729.23) * mm});
            skLineSegment(sketch, "E244.MirrorCS", {"start": v(-776.35, -711.2) * mm, "end": v(-827.15, -711.2) * mm});
            skLineSegment(sketch, "E245.MirrorCS", {"start": v(-758.32, -711.2) * mm, "end": v(-707.52, -711.2) * mm});
            skLineSegment(sketch, "E246.MirrorCS", {"start": v(-758.32, -787.4) * mm, "end": v(-758.32, -711.2) * mm});
            skLineSegment(sketch, "E247.MirrorCS", {"start": v(-776.35, -787.4) * mm, "end": v(-758.32, -787.4) * mm});
            skLineSegment(sketch, "E248.MirrorCS", {"start": v(-758.32, -1828.8) * mm, "end": v(-758.32, -1810.77) * mm});
            skLineSegment(sketch, "E249.MirrorCS", {"start": v(-776.35, -1828.8) * mm, "end": v(-758.32, -1828.8) * mm});
            skLineSegment(sketch, "E250.MirrorCS", {"start": v(-776.35, -1828.8) * mm, "end": v(-776.35, -1810.77) * mm});
            skLineSegment(sketch, "E251.MirrorCS", {"start": v(-776.35, -1574.8) * mm, "end": v(-758.32, -1574.8) * mm});
            skLineSegment(sketch, "E252.MirrorCS", {"start": v(-776.35, -1752.6) * mm, "end": v(-758.32, -1752.6) * mm});
            skLineSegment(sketch, "E253.MirrorCS", {"start": v(-827.15, -1828.8) * mm, "end": v(-827.15, -1810.77) * mm});
            skLineSegment(sketch, "E254.MirrorCS", {"start": v(-758.32, -1828.8) * mm, "end": v(-758.32, -1752.6) * mm});
            skLineSegment(sketch, "E255.MirrorCS", {"start": v(-758.32, -1828.8) * mm, "end": v(-707.52, -1828.8) * mm});
            skLineSegment(sketch, "E256.MirrorCS", {"start": v(-758.32, -1810.77) * mm, "end": v(-707.52, -1810.77) * mm});
            skLineSegment(sketch, "E257.MirrorCS", {"start": v(-776.35, -1358.9) * mm, "end": v(-758.32, -1358.9) * mm});
            skLineSegment(sketch, "E258.MirrorCS", {"start": v(-707.52, -1828.8) * mm, "end": v(-707.52, -1810.77) * mm});
            skLineSegment(sketch, "E259.MirrorCS", {"start": v(-776.35, -1181.1) * mm, "end": v(-758.32, -1181.1) * mm});
            skLineSegment(sketch, "E260.MirrorCS", {"start": v(-776.35, -1828.8) * mm, "end": v(-776.35, -1752.6) * mm});
            skLineSegment(sketch, "E261.MirrorCS", {"start": v(-776.35, -1828.8) * mm, "end": v(-827.15, -1828.8) * mm});
            skLineSegment(sketch, "E262.MirrorCS", {"start": v(-776.35, -965.2) * mm, "end": v(-758.32, -965.2) * mm});
            skLineSegment(sketch, "E263.MirrorCS", {"start": v(-776.35, -1810.77) * mm, "end": v(-827.15, -1810.77) * mm});
            skPoint(sketch, "E264.MirrorP", {"position": v(-758.32, -1663.7) * mm});
            skLineSegment(sketch, "E265.MirrorCS", {"start": v(-776.35, -1574.8) * mm, "end": v(-776.35, -1358.9) * mm});
            skLineSegment(sketch, "E266.MirrorCS", {"start": v(-758.32, -1574.8) * mm, "end": v(-758.32, -1358.9) * mm});
            skLineSegment(sketch, "E267.MirrorCS", {"start": v(-758.32, -1181.1) * mm, "end": v(-758.32, -965.2) * mm});
            skLineSegment(sketch, "E268.MirrorCS", {"start": v(-776.35, -1181.1) * mm, "end": v(-776.35, -965.2) * mm});
            skLineSegment(sketch, "E269.MirrorCS", {"start": v(-758.32, -1752.6) * mm, "end": v(-758.32, -1574.8) * mm, "construction": true});
            skPoint(sketch, "E270.MirrorP", {"position": v(-767.33, -1828.8) * mm});
            skLineSegment(sketch, "E271", {"start": v(-925.07, 0) * mm, "end": v(-776.35, 0) * mm, "construction": true});
            skPoint(sketch, "E272", {"position": v(-850.7, 0) * mm});
            skLineSegment(sketch, "E273.bottom", {"start": v(-868.93, -1250.95) * mm, "end": v(-665.73, -1250.95) * mm});
            skLineSegment(sketch, "E273.top", {"start": v(-868.93, -1289.05) * mm, "end": v(-665.73, -1289.05) * mm});
            skLineSegment(sketch, "E273.left", {"start": v(-868.93, -1250.95) * mm, "end": v(-868.93, -1289.05) * mm});
            skLineSegment(sketch, "E273.right", {"start": v(-665.73, -1250.95) * mm, "end": v(-665.73, -1289.05) * mm});
            skPoint(sketch, "E273.middle", {"position": v(-767.33, -1270) * mm});
            skLineSegment(sketch, "E274.bottom", {"start": v(-856.23, 19.05) * mm, "end": v(-678.43, 19.05) * mm});
            skLineSegment(sketch, "E274.top", {"start": v(-856.23, -19.05) * mm, "end": v(-678.43, -19.05) * mm});
            skLineSegment(sketch, "E274.left", {"start": v(-856.23, 19.05) * mm, "end": v(-856.23, -19.05) * mm});
            skLineSegment(sketch, "E274.right", {"start": v(-678.43, 19.05) * mm, "end": v(-678.43, -19.05) * mm});
            skPoint(sketch, "E274.middle", {"position": v(-767.33, 0) * mm});
            skLineSegment(sketch, "E275", {"start": v(-441.32, -928.37) * mm, "end": v(-441.32, -711.2) * mm});
            skLineSegment(sketch, "E276", {"start": v(-441.32, -711.2) * mm, "end": v(-415.92, -711.2) * mm});
            skLineSegment(sketch, "E277", {"start": v(-415.92, -711.2) * mm, "end": v(-415.92, -928.37) * mm});
            skLineSegment(sketch, "E278", {"start": v(-441.32, -1791.97) * mm, "end": v(-441.32, -1828.8) * mm});
            skLineSegment(sketch, "E279", {"start": v(-441.32, -1828.8) * mm, "end": v(-415.92, -1828.8) * mm});
            skLineSegment(sketch, "E280", {"start": v(-415.92, -1828.8) * mm, "end": v(-415.92, -1791.97) * mm});
            skSolve(sketch);
        }
        {
            var Q0;
            {var subQ1=sQuery(id+"F1.wireOp",EDGE,"E60.bottom");Q0=makeQuery(id+"F1.imprint","IMPRINT",FACE,{"disambiguationData":[TD([[makeQuery(id+"F1.imprint","IMPRINT",EDGE,{"derivedFrom":subQ1}),-1.0]])]});}
            var Q1;
            Q1=makeQuery(id+"F1.imprint","IMPRINT",FACE,{"disambiguationData":[TD([[makeQuery(id+"F1.imprint","IMPRINT",EDGE,{"derivedFrom":sQuery(id+"F1.wireOp",EDGE,"E61.bottom")}),-1.0]])]});
            var Q2;
            Q2=makeQuery(id+"F1.imprint","IMPRINT",FACE,{"disambiguationData":[TD([[makeQuery(id+"F1.imprint","IMPRINT",EDGE,{"derivedFrom":sQuery(id+"F1.wireOp",EDGE,"E62.bottom")}),1.0]])]});
            var Q3;
            Q3=makeQuery(id+"F1.imprint","IMPRINT",FACE,{"disambiguationData":[TD([[makeQuery(id+"F1.imprint","IMPRINT",EDGE,{"derivedFrom":sQuery(id+"F1.wireOp",EDGE,"E70.MirrorCS")}),1.0]])]});
            var Q4;
            Q4=makeQuery(id+"F1.imprint","IMPRINT",FACE,{"disambiguationData":[TD([[makeQuery(id+"F1.imprint","IMPRINT",EDGE,{"derivedFrom":sQuery(id+"F1.wireOp",EDGE,"E74.MirrorCS")}),1.0]])]});
            var Q5;
            {var subQ33=sQuery(id+"F1.wireOp",EDGE,"E1.bottom");Q5=makeQuery(id+"F1.imprint","IMPRINT",FACE,{"disambiguationData":[TD([[makeQuery(id+"F1.imprint","IMPRINT",EDGE,{"derivedFrom":subQ33}),1.0]])]});}
            var Q6;
            {var subQ3=sQuery(id+"F1.wireOp",EDGE,"E86.MirrorCS");Q6=makeQuery(id+"F1.imprint","IMPRINT",FACE,{"disambiguationData":[TD([[makeQuery(id+"F1.imprint","IMPRINT",EDGE,{"derivedFrom":subQ3}),1.0]])]});}
            var Q7;
            {var subQ0=sQuery(id+"F1.wireOp",EDGE,"E97.MirrorCS");Q7=makeQuery(id+"F1.imprint","IMPRINT",FACE,{"disambiguationData":[TD([[makeQuery(id+"F1.imprint","IMPRINT",EDGE,{"derivedFrom":subQ0}),1.0]])]});}
            var Q8;
            {var subQ0=sQuery(id+"F1.wireOp",EDGE,"E103.MirrorCS");Q8=makeQuery(id+"F1.imprint","IMPRINT",FACE,{"disambiguationData":[TD([[makeQuery(id+"F1.imprint","IMPRINT",EDGE,{"derivedFrom":subQ0}),-1.0]])]});}
            var Q9;
            Q9=makeQuery(id+"F1.imprint","IMPRINT",FACE,{"disambiguationData":[TD([[makeQuery(id+"F1.imprint","IMPRINT",EDGE,{"derivedFrom":sQuery(id+"F1.wireOp",EDGE,"57e3e2d5-9861-4d4a-b3b2-66642197ff7910.MirrorCS")}),1.0]])]});
            var Q10;
            Q10=makeQuery(id+"F1.imprint","IMPRINT",FACE,{"disambiguationData":[TD([[makeQuery(id+"F1.imprint","IMPRINT",EDGE,{"derivedFrom":sQuery(id+"F1.wireOp",EDGE,"a349733f-2b55-4632-b4a8-78e4d935735f8.MirrorCS")}),-1.0]])]});
            var Q11;
            {var subQ10=sQuery(id+"F1.wireOp",EDGE,"E176.bottom");Q11=makeQuery(id+"F1.imprint","IMPRINT",FACE,{"disambiguationData":[TD([[makeQuery(id+"F1.imprint","IMPRINT",EDGE,{"derivedFrom":subQ10}),-1.0]])]});}
            var Q12;
            {var subQ0=sQuery(id+"F1.wireOp",EDGE,"VmXK4Q5d-QqvZ-Wuxc-wU44-PQGpzSBKFl6L");Q12=makeQuery(id+"F1.imprint","IMPRINT",FACE,{"disambiguationData":[TD([[makeQuery(id+"F1.imprint","IMPRINT",EDGE,{"derivedFrom":subQ0}),-1.0]])]});}
            var Q13;
            {var subQ0=sQuery(id+"F1.wireOp",EDGE,"vC60dyBu-nMOn-iXCW-ycnC-LK4FzoJF3nVa");Q13=makeQuery(id+"F1.imprint","IMPRINT",FACE,{"disambiguationData":[TD([[makeQuery(id+"F1.imprint","IMPRINT",EDGE,{"derivedFrom":subQ0}),-1.0]])]});}
            var Q14;
            {var subQ0=sQuery(id+"F1.wireOp",EDGE,"E230");Q14=makeQuery(id+"F1.imprint","IMPRINT",FACE,{"disambiguationData":[TD([[makeQuery(id+"F1.imprint","IMPRINT",EDGE,{"derivedFrom":subQ0}),1.0]])]});}
            var Q15;
            {var subQ0=sQuery(id+"F1.wireOp",EDGE,"E233");Q15=makeQuery(id+"F1.imprint","IMPRINT",FACE,{"disambiguationData":[TD([[makeQuery(id+"F1.imprint","IMPRINT",EDGE,{"derivedFrom":subQ0}),-1.0]])]});}
            var Q16;
            {var subQ3=sQuery(id+"F1.wireOp",EDGE,"E220.bottom");Q16=makeQuery(id+"F1.imprint","IMPRINT",FACE,{"disambiguationData":[TD([[makeQuery(id+"F1.imprint","IMPRINT",EDGE,{"derivedFrom":subQ3}),-1.0]])]});}
            var Q17;
            {var subQ0=sQuery(id+"F1.wireOp",EDGE,"cDKuqHaH-8n5U-EMem-4c86-sEQc4i5HatKE");Q17=makeQuery(id+"F1.imprint","IMPRINT",FACE,{"disambiguationData":[TD([[makeQuery(id+"F1.imprint","IMPRINT",EDGE,{"derivedFrom":subQ0}),1.0]])]});}
            var Q18;
            {var subQ0=sQuery(id+"F1.wireOp",EDGE,"E227");Q18=makeQuery(id+"F1.imprint","IMPRINT",FACE,{"disambiguationData":[TD([[makeQuery(id+"F1.imprint","IMPRINT",EDGE,{"derivedFrom":subQ0}),1.0]])]});}
            var Q19;
            Q19=makeQuery(id+"F1.imprint","IMPRINT",FACE,{"disambiguationData":[TD([[makeQuery(id+"F1.imprint","IMPRINT",EDGE,{"derivedFrom":sQuery(id+"F1.wireOp",EDGE,"E44.top")}),-1.0]])]});
            var Q20;
            Q20=makeQuery(id+"F1.imprint","IMPRINT",FACE,{"disambiguationData":[TD([[makeQuery(id+"F1.imprint","IMPRINT",EDGE,{"derivedFrom":sQuery(id+"F1.wireOp",EDGE,"E220.bottom")}),1.0]])]});
            var Q21;
            Q21=makeQuery(id+"F1.imprint","IMPRINT",FACE,{"disambiguationData":[TD([[makeQuery(id+"F1.imprint","IMPRINT",EDGE,{"derivedFrom":sQuery(id+"F1.wireOp",EDGE,"E220.top")}),-1.0]])]});
            extrude(context, id + "F2", {"entities" : qUnion([Q0, Q1, Q2, Q3, Q4, Q5, Q6, Q7, Q8, Q9, Q10, Q11, Q12, Q13, Q14, Q15, Q16, Q17, Q18, Q19, Q20, Q21]), "depth" : (getVariable(context, 'ply34')) * mm});
        }
        {
            var Q0;
            {var subQ6=sQuery(id+"F1.wireOp",EDGE,"E160.bottom");Q0=makeQuery(id+"F1.imprint","IMPRINT",FACE,{"disambiguationData":[TD([[makeQuery(id+"F1.imprint","IMPRINT",EDGE,{"derivedFrom":subQ6}),-1.0]])]});}
            var Q1;
            {var subQ0=sQuery(id+"F1.wireOp",EDGE,"E166");Q1=makeQuery(id+"F1.imprint","IMPRINT",FACE,{"disambiguationData":[TD([[makeQuery(id+"F1.imprint","IMPRINT",EDGE,{"derivedFrom":subQ0}),-1.0]])]});}
            var Q2;
            {var subQ0=sQuery(id+"F1.wireOp",EDGE,"E163");Q2=makeQuery(id+"F1.imprint","IMPRINT",FACE,{"disambiguationData":[TD([[makeQuery(id+"F1.imprint","IMPRINT",EDGE,{"derivedFrom":subQ0}),-1.0]])]});}
            var Q3;
            {var subQ0=sQuery(id+"F1.wireOp",EDGE,"E169");Q3=makeQuery(id+"F1.imprint","IMPRINT",FACE,{"disambiguationData":[TD([[makeQuery(id+"F1.imprint","IMPRINT",EDGE,{"derivedFrom":subQ0}),-1.0]])]});}
            var Q4;
            {var subQ0=sQuery(id+"F1.wireOp",EDGE,"E172");Q4=makeQuery(id+"F1.imprint","IMPRINT",FACE,{"disambiguationData":[TD([[makeQuery(id+"F1.imprint","IMPRINT",EDGE,{"derivedFrom":subQ0}),-1.0]])]});}
            extrude(context, id + "F3", {"entities" : qUnion([Q0, Q1, Q2, Q3, Q4]), "depth" : 12.2 * mm});
        }
        {
            var Q0;
            Q0=makeQuery(id+"F1.imprint","IMPRINT",FACE,{"disambiguationData":[TD([[makeQuery(id+"F1.imprint","IMPRINT",EDGE,{"derivedFrom":sQuery(id+"F1.wireOp",EDGE,"c5a33fef-cf20-4e9f-8e37-3778fd242a644.MirrorCS")}),1.0]])]});
            var Q1;
            Q1=makeQuery(id+"F1.imprint","IMPRINT",FACE,{"disambiguationData":[TD([[makeQuery(id+"F1.imprint","IMPRINT",EDGE,{"derivedFrom":sQuery(id+"F1.wireOp",EDGE,"E123.MirrorCS")}),1.0]])]});
            var Q2;
            Q2=makeQuery(id+"F1.imprint","IMPRINT",FACE,{"disambiguationData":[TD([[makeQuery(id+"F1.imprint","IMPRINT",EDGE,{"derivedFrom":sQuery(id+"F1.wireOp",EDGE,"E115.bottom")}),1.0]])]});
            var Q3;
            Q3=makeQuery(id+"F1.imprint","IMPRINT",FACE,{"disambiguationData":[TD([[makeQuery(id+"F1.imprint","IMPRINT",EDGE,{"derivedFrom":sQuery(id+"F1.wireOp",EDGE,"E112.bottom")}),1.0]])]});
            var Q4;
            Q4=makeQuery(id+"F1.imprint","IMPRINT",FACE,{"disambiguationData":[TD([[makeQuery(id+"F1.imprint","IMPRINT",EDGE,{"derivedFrom":sQuery(id+"F1.wireOp",EDGE,"E125.MirrorCS")}),1.0]])]});
            var Q5;
            Q5=makeQuery(id+"F1.imprint","IMPRINT",FACE,{"disambiguationData":[TD([[makeQuery(id+"F1.imprint","IMPRINT",EDGE,{"derivedFrom":sQuery(id+"F1.wireOp",EDGE,"c5a33fef-cf20-4e9f-8e37-3778fd242a642.MirrorCS")}),-1.0]])]});
            var Q6;
            Q6=makeQuery(id+"F1.imprint","IMPRINT",FACE,{"disambiguationData":[TD([[makeQuery(id+"F1.imprint","IMPRINT",EDGE,{"derivedFrom":sQuery(id+"F1.wireOp",EDGE,"c5a33fef-cf20-4e9f-8e37-3778fd242a640.MirrorCS")}),-1.0]])]});
            var Q7;
            Q7=makeQuery(id+"F1.imprint","IMPRINT",FACE,{"disambiguationData":[TD([[makeQuery(id+"F1.imprint","IMPRINT",EDGE,{"derivedFrom":sQuery(id+"F1.wireOp",EDGE,"E121.MirrorCS")}),-1.0]])]});
            var Q8;
            Q8=makeQuery(id+"F1.imprint","IMPRINT",FACE,{"disambiguationData":[TD([[makeQuery(id+"F1.imprint","IMPRINT",EDGE,{"derivedFrom":sQuery(id+"F1.wireOp",EDGE,"E116.MirrorCS")}),-1.0]])]});
            extrude(context, id + "F4", {"entities" : qUnion([Q0, Q1, Q2, Q3, Q4, Q5, Q6, Q7, Q8]), "operationType" : NewBodyOperationType.ADD, "depth" : (getVariable(context, 'ply34') - .129) * mm});
        }
    });
